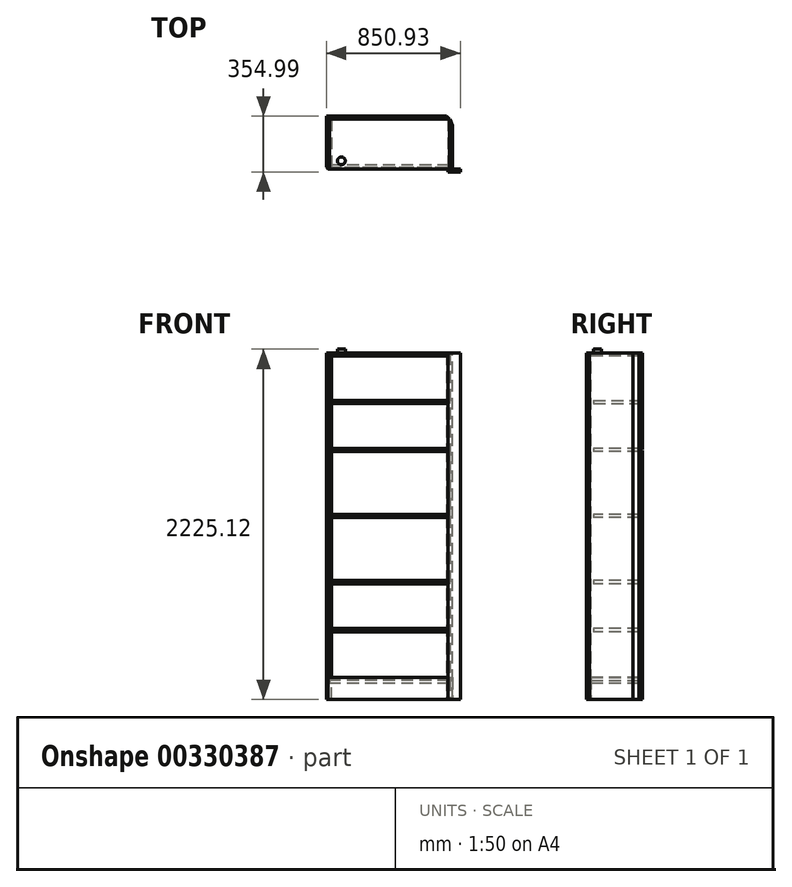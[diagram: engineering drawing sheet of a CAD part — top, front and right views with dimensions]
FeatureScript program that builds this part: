
annotation { "Feature Type Name" : "Feature", "Feature Type Description" : "" }
export const myFeature = defineFeature(function(context is Context, id is Id, definition is map)
    precondition{}
    {
        {
            var Q0;
            Q0=qCreatedBy(makeId("Right.planeOp"),FACE);
            var sketch = newSketch(context, id + "F0", { "sketchPlane" : qUnion([Q0])});
            skLineSegment(sketch, "E0.bottom", {"start": v(175, -1100) * mm, "end": v(-175, -1100) * mm});
            skLineSegment(sketch, "E0.top", {"start": v(175, 1100) * mm, "end": v(-175, 1100) * mm});
            skLineSegment(sketch, "E0.left", {"start": v(175, -1100) * mm, "end": v(175, 1100) * mm});
            skLineSegment(sketch, "E0.right", {"start": v(-175, -1100) * mm, "end": v(-175, 1100) * mm});
            skPoint(sketch, "E0.middle", {"position": v(0, 0) * mm});
            skSolve(sketch);
        }
        {
            var Q0;
            Q0=makeQuery(id+"F0.imprint","IMPRINT",FACE,{"disambiguationData":[TD([[makeQuery(id+"F0.imprint","IMPRINT",EDGE,{"derivedFrom":sQuery(id+"F0.wireOp",EDGE,"E0.bottom")}),-1.0]])]});
            extrude(context, id + "F1", {"entities" : qUnion([Q0]), "endBound" : BoundingType.SYMMETRIC, "depth" : 30 * mm});
        }
        {
            var Q0;
            Q0=makeQuery(id+"F1.opExtrude","SWEPT_BODY",BODY,{"disambiguationData":[OSD([sQuery(id+"F0.wireOp",EDGE,"E0.bottom"),sQuery(id+"F0.wireOp",EDGE,"E0.top"),sQuery(id+"F0.wireOp",EDGE,"E0.left"),sQuery(id+"F0.wireOp",EDGE,"E0.right")])]});
            transform(context, id + "F2", {"entities" : qUnion([Q0]), "transformType" : TransformType.TRANSLATION_3D, "dx" : -740 * mm, "dy" : 0 * mm, "dz" : 0 * mm, "makeCopy" : true});
        }
        {
            var Q0;
            Q0=makeQuery(id+"F2.opPattern","COPY",BODY,{"derivedFrom":makeQuery(id+"F1.opExtrude","SWEPT_BODY",BODY,{"disambiguationData":[OSD([sQuery(id+"F0.wireOp",EDGE,"E0.bottom"),sQuery(id+"F0.wireOp",EDGE,"E0.top"),sQuery(id+"F0.wireOp",EDGE,"E0.left"),sQuery(id+"F0.wireOp",EDGE,"E0.right")])]}),"instanceName":"1"});
            transform(context, id + "F3", {"entities" : qUnion([Q0]), "transformType" : TransformType.TRANSLATION_3D, "dx" : -30 * mm, "dy" : 0 * mm, "dz" : 0 * mm, "makeCopy" : false});
        }
        {
            var Q0;
            Q0=makeQuery(id+"F1.opExtrude","SWEPT_BODY",BODY,{"disambiguationData":[OSD([sQuery(id+"F0.wireOp",EDGE,"E0.bottom"),sQuery(id+"F0.wireOp",EDGE,"E0.top"),sQuery(id+"F0.wireOp",EDGE,"E0.left"),sQuery(id+"F0.wireOp",EDGE,"E0.right")])]});
            var Q1;
            Q1=makeQuery(id+"F2.opPattern","COPY",BODY,{"derivedFrom":makeQuery(id+"F1.opExtrude","SWEPT_BODY",BODY,{"disambiguationData":[OSD([sQuery(id+"F0.wireOp",EDGE,"E0.bottom"),sQuery(id+"F0.wireOp",EDGE,"E0.top"),sQuery(id+"F0.wireOp",EDGE,"E0.left"),sQuery(id+"F0.wireOp",EDGE,"E0.right")])]}),"instanceName":"1"});
            transform(context, id + "F4", {"entities" : qUnion([Q0, Q1]), "transformType" : TransformType.TRANSLATION_3D, "dx" : 385 * mm, "dy" : 0 * mm, "dz" : 0 * mm, "makeCopy" : false});
        }
        {
            var Q0;
            Q0=qCreatedBy(makeId("Top.planeOp"),FACE);
            var sketch = newSketch(context, id + "F5", { "sketchPlane" : qUnion([Q0])});
            skLineSegment(sketch, "E1.bottom", {"start": v(380, -175) * mm, "end": v(-380, -175) * mm});
            skLineSegment(sketch, "E1.top", {"start": v(380, 175) * mm, "end": v(-380, 175) * mm});
            skLineSegment(sketch, "E1.left", {"start": v(380, -175) * mm, "end": v(380, 175) * mm});
            skLineSegment(sketch, "E1.right", {"start": v(-380, -175) * mm, "end": v(-380, 175) * mm});
            skPoint(sketch, "E1.middle", {"position": v(0, 0) * mm});
            skSolve(sketch);
        }
        {
            var Q0;
            Q0=makeQuery(id+"F5.imprint","IMPRINT",FACE,{"disambiguationData":[TD([[makeQuery(id+"F5.imprint","IMPRINT",EDGE,{"derivedFrom":sQuery(id+"F5.wireOp",EDGE,"E1.bottom")}),-1.0]])]});
            extrude(context, id + "F6", {"entities" : qUnion([Q0]), "depth" : 20 * mm});
        }
        {
            var Q0;
            Q0=qCreatedBy(makeId("Top.planeOp"),FACE);
            var sketch = newSketch(context, id + "F7", { "sketchPlane" : qUnion([Q0])});
            skLineSegment(sketch, "E2.bottom", {"start": v(380, -175) * mm, "end": v(-380, -175) * mm});
            skLineSegment(sketch, "E2.top", {"start": v(380, 175) * mm, "end": v(-380, 175) * mm});
            skLineSegment(sketch, "E2.left", {"start": v(380, -175) * mm, "end": v(380, 175) * mm});
            skLineSegment(sketch, "E2.right", {"start": v(-380, -175) * mm, "end": v(-380, 175) * mm});
            skPoint(sketch, "E2.middle", {"position": v(0, 0) * mm});
            skSolve(sketch);
        }
        {
            var Q0;
            Q0=makeQuery(id+"F7.imprint","IMPRINT",FACE,{"disambiguationData":[TD([[makeQuery(id+"F7.imprint","IMPRINT",EDGE,{"derivedFrom":sQuery(id+"F7.wireOp",EDGE,"E2.bottom")}),-1.0]])]});
            extrude(context, id + "F8", {"entities" : qUnion([Q0]), "depth" : 20 * mm});
        }
        {
            var Q0;
            Q0=makeQuery(id+"F8.opExtrude","SWEPT_BODY",BODY,{"disambiguationData":[OSD([sQuery(id+"F7.wireOp",EDGE,"E2.bottom"),sQuery(id+"F7.wireOp",EDGE,"E2.top"),sQuery(id+"F7.wireOp",EDGE,"E2.left"),sQuery(id+"F7.wireOp",EDGE,"E2.right")])]});
            transform(context, id + "F9", {"entities" : qUnion([Q0]), "transformType" : TransformType.TRANSLATION_3D, "dx" : 0 * mm, "dy" : 0 * mm, "dz" : -980 * mm, "makeCopy" : false});
        }
        {
            var Q0;
            Q0=makeQuery(id+"F8.opExtrude","SWEPT_BODY",BODY,{"disambiguationData":[OSD([sQuery(id+"F7.wireOp",EDGE,"E2.bottom"),sQuery(id+"F7.wireOp",EDGE,"E2.top"),sQuery(id+"F7.wireOp",EDGE,"E2.left"),sQuery(id+"F7.wireOp",EDGE,"E2.right")])]});
            transform(context, id + "F10", {"entities" : qUnion([Q0]), "transformType" : TransformType.TRANSLATION_3D, "dx" : 0 * mm, "dy" : 0 * mm, "dz" : 300 * mm, "makeCopy" : false});
        }
        {
            var Q0;
            Q0=makeQuery(id+"F8.opExtrude","SWEPT_BODY",BODY,{"disambiguationData":[OSD([sQuery(id+"F7.wireOp",EDGE,"E2.bottom"),sQuery(id+"F7.wireOp",EDGE,"E2.top"),sQuery(id+"F7.wireOp",EDGE,"E2.left"),sQuery(id+"F7.wireOp",EDGE,"E2.right")])]});
            transform(context, id + "F11", {"entities" : qUnion([Q0]), "transformType" : TransformType.TRANSLATION_3D, "dx" : 0 * mm, "dy" : 0 * mm, "dz" : 400 * mm, "makeCopy" : false});
        }
        {
            var Q0;
            Q0=makeQuery(id+"F8.opExtrude","SWEPT_BODY",BODY,{"disambiguationData":[OSD([sQuery(id+"F7.wireOp",EDGE,"E2.bottom"),sQuery(id+"F7.wireOp",EDGE,"E2.top"),sQuery(id+"F7.wireOp",EDGE,"E2.left"),sQuery(id+"F7.wireOp",EDGE,"E2.right")])]});
            transform(context, id + "F12", {"entities" : qUnion([Q0]), "transformType" : TransformType.TRANSLATION_3D, "dx" : 0 * mm, "dy" : 0 * mm, "dz" : 300 * mm, "makeCopy" : false});
        }
        {
            var Q0;
            Q0=makeQuery(id+"F8.opExtrude","SWEPT_BODY",BODY,{"disambiguationData":[OSD([sQuery(id+"F7.wireOp",EDGE,"E2.bottom"),sQuery(id+"F7.wireOp",EDGE,"E2.top"),sQuery(id+"F7.wireOp",EDGE,"E2.left"),sQuery(id+"F7.wireOp",EDGE,"E2.right")])]});
            transform(context, id + "F13", {"entities" : qUnion([Q0]), "transformType" : TransformType.TRANSLATION_3D, "dx" : 0 * mm, "dy" : 0 * mm, "dz" : 300 * mm, "makeCopy" : false});
        }
        {
            var Q0;
            Q0=makeQuery(id+"F8.opExtrude","SWEPT_BODY",BODY,{"disambiguationData":[OSD([sQuery(id+"F7.wireOp",EDGE,"E2.bottom"),sQuery(id+"F7.wireOp",EDGE,"E2.top"),sQuery(id+"F7.wireOp",EDGE,"E2.left"),sQuery(id+"F7.wireOp",EDGE,"E2.right")])]});
            transform(context, id + "F14", {"entities" : qUnion([Q0]), "transformType" : TransformType.TRANSLATION_3D, "dx" : 0 * mm, "dy" : 0 * mm, "dz" : 400 * mm, "makeCopy" : false});
        }
        {
            var Q0;
            Q0=makeQuery(id+"F8.opExtrude","SWEPT_BODY",BODY,{"disambiguationData":[OSD([sQuery(id+"F7.wireOp",EDGE,"E2.bottom"),sQuery(id+"F7.wireOp",EDGE,"E2.top"),sQuery(id+"F7.wireOp",EDGE,"E2.left"),sQuery(id+"F7.wireOp",EDGE,"E2.right")])]});
            transform(context, id + "F15", {"entities" : qUnion([Q0]), "transformType" : TransformType.TRANSLATION_3D, "dx" : 0 * mm, "dy" : 0 * mm, "dz" : 360 * mm, "makeCopy" : false});
        }
        {
            var Q0;
            Q0=makeQuery(id+"F8.opExtrude","SWEPT_BODY",BODY,{"disambiguationData":[OSD([sQuery(id+"F7.wireOp",EDGE,"E2.bottom"),sQuery(id+"F7.wireOp",EDGE,"E2.top"),sQuery(id+"F7.wireOp",EDGE,"E2.left"),sQuery(id+"F7.wireOp",EDGE,"E2.right")])]});
            transform(context, id + "F16", {"entities" : qUnion([Q0]), "transformType" : TransformType.TRANSLATION_3D, "dx" : 0 * mm, "dy" : 0 * mm, "dz" : -2060 * mm, "makeCopy" : true});
        }
        {
            var Q0;
            Q0=makeQuery(id+"F6.opExtrude","SWEPT_BODY",BODY,{"disambiguationData":[OSD([sQuery(id+"F5.wireOp",EDGE,"E1.bottom"),sQuery(id+"F5.wireOp",EDGE,"E1.top"),sQuery(id+"F5.wireOp",EDGE,"E1.left"),sQuery(id+"F5.wireOp",EDGE,"E1.right")])]});
            transform(context, id + "F17", {"entities" : qUnion([Q0]), "transformType" : TransformType.TRANSLATION_3D, "dx" : 0 * mm, "dy" : 25 * mm, "dz" : 779.46 * mm, "makeCopy" : false});
        }
        {
            var Q0;
            Q0=makeQuery(id+"F8.opExtrude","SWEPT_BODY",BODY,{"disambiguationData":[OSD([sQuery(id+"F7.wireOp",EDGE,"E2.bottom"),sQuery(id+"F7.wireOp",EDGE,"E2.top"),sQuery(id+"F7.wireOp",EDGE,"E2.left"),sQuery(id+"F7.wireOp",EDGE,"E2.right")])]});
            var Q1;
            Q1=makeQuery(id+"F1.opExtrude","SWEPT_BODY",BODY,{"disambiguationData":[OSD([sQuery(id+"F0.wireOp",EDGE,"E0.bottom"),sQuery(id+"F0.wireOp",EDGE,"E0.top"),sQuery(id+"F0.wireOp",EDGE,"E0.left"),sQuery(id+"F0.wireOp",EDGE,"E0.right")])]});
            var Q2;
            Q2=makeQuery(id+"F2.opPattern","COPY",BODY,{"derivedFrom":makeQuery(id+"F1.opExtrude","SWEPT_BODY",BODY,{"disambiguationData":[OSD([sQuery(id+"F0.wireOp",EDGE,"E0.bottom"),sQuery(id+"F0.wireOp",EDGE,"E0.top"),sQuery(id+"F0.wireOp",EDGE,"E0.left"),sQuery(id+"F0.wireOp",EDGE,"E0.right")])]}),"instanceName":"1"});
            booleanBodies(context, id + "F18", {"operationType" : BooleanOperationType.SUBTRACTION, "tools" : qUnion([Q0]), "targets" : qUnion([Q1, Q2]), "keepTools" : true});
        }
        {
            var Q0;
            Q0=makeQuery(id+"F16.opPattern","COPY",BODY,{"derivedFrom":makeQuery(id+"F8.opExtrude","SWEPT_BODY",BODY,{"disambiguationData":[OSD([sQuery(id+"F7.wireOp",EDGE,"E2.bottom"),sQuery(id+"F7.wireOp",EDGE,"E2.top"),sQuery(id+"F7.wireOp",EDGE,"E2.left"),sQuery(id+"F7.wireOp",EDGE,"E2.right")])]}),"instanceName":"1"});
            var Q1;
            Q1=makeQuery(id+"F1.opExtrude","SWEPT_BODY",BODY,{"disambiguationData":[OSD([sQuery(id+"F0.wireOp",EDGE,"E0.bottom"),sQuery(id+"F0.wireOp",EDGE,"E0.top"),sQuery(id+"F0.wireOp",EDGE,"E0.left"),sQuery(id+"F0.wireOp",EDGE,"E0.right")])]});
            var Q2;
            Q2=makeQuery(id+"F2.opPattern","COPY",BODY,{"derivedFrom":makeQuery(id+"F1.opExtrude","SWEPT_BODY",BODY,{"disambiguationData":[OSD([sQuery(id+"F0.wireOp",EDGE,"E0.bottom"),sQuery(id+"F0.wireOp",EDGE,"E0.top"),sQuery(id+"F0.wireOp",EDGE,"E0.left"),sQuery(id+"F0.wireOp",EDGE,"E0.right")])]}),"instanceName":"1"});
            booleanBodies(context, id + "F19", {"operationType" : BooleanOperationType.SUBTRACTION, "tools" : qUnion([Q0]), "targets" : qUnion([Q1, Q2]), "keepTools" : true});
        }
        {
            var Q0;
            Q0=makeQuery(id+"F6.opExtrude","SWEPT_BODY",BODY,{"disambiguationData":[OSD([sQuery(id+"F5.wireOp",EDGE,"E1.bottom"),sQuery(id+"F5.wireOp",EDGE,"E1.top"),sQuery(id+"F5.wireOp",EDGE,"E1.left"),sQuery(id+"F5.wireOp",EDGE,"E1.right")])]});
            var Q1;
            Q1=makeQuery(id+"F1.opExtrude","SWEPT_BODY",BODY,{"disambiguationData":[OSD([sQuery(id+"F0.wireOp",EDGE,"E0.bottom"),sQuery(id+"F0.wireOp",EDGE,"E0.top"),sQuery(id+"F0.wireOp",EDGE,"E0.left"),sQuery(id+"F0.wireOp",EDGE,"E0.right")])]});
            var Q2;
            Q2=makeQuery(id+"F2.opPattern","COPY",BODY,{"derivedFrom":makeQuery(id+"F1.opExtrude","SWEPT_BODY",BODY,{"disambiguationData":[OSD([sQuery(id+"F0.wireOp",EDGE,"E0.bottom"),sQuery(id+"F0.wireOp",EDGE,"E0.top"),sQuery(id+"F0.wireOp",EDGE,"E0.left"),sQuery(id+"F0.wireOp",EDGE,"E0.right")])]}),"instanceName":"1"});
            booleanBodies(context, id + "F20", {"operationType" : BooleanOperationType.SUBTRACTION, "tools" : qUnion([Q0]), "targets" : qUnion([Q1, Q2]), "keepTools" : true});
        }
        {
            var Q0;
            Q0=makeQuery(id+"F6.opExtrude","SWEPT_BODY",BODY,{"disambiguationData":[OSD([sQuery(id+"F5.wireOp",EDGE,"E1.bottom"),sQuery(id+"F5.wireOp",EDGE,"E1.top"),sQuery(id+"F5.wireOp",EDGE,"E1.left"),sQuery(id+"F5.wireOp",EDGE,"E1.right")])]});
            transform(context, id + "F21", {"entities" : qUnion([Q0]), "transformType" : TransformType.TRANSLATION_3D, "dx" : 0 * mm, "dy" : 0 * mm, "dz" : -305 * mm, "makeCopy" : true});
        }
        {
            var Q0;
            Q0=makeQuery(id+"F21.opPattern","COPY",BODY,{"derivedFrom":makeQuery(id+"F6.opExtrude","SWEPT_BODY",BODY,{"disambiguationData":[OSD([sQuery(id+"F5.wireOp",EDGE,"E1.bottom"),sQuery(id+"F5.wireOp",EDGE,"E1.top"),sQuery(id+"F5.wireOp",EDGE,"E1.left"),sQuery(id+"F5.wireOp",EDGE,"E1.right")])]}),"instanceName":"1"});
            var Q1;
            Q1=makeQuery(id+"F2.opPattern","COPY",BODY,{"derivedFrom":makeQuery(id+"F1.opExtrude","SWEPT_BODY",BODY,{"disambiguationData":[OSD([sQuery(id+"F0.wireOp",EDGE,"E0.bottom"),sQuery(id+"F0.wireOp",EDGE,"E0.top"),sQuery(id+"F0.wireOp",EDGE,"E0.left"),sQuery(id+"F0.wireOp",EDGE,"E0.right")])]}),"instanceName":"1"});
            var Q2;
            Q2=makeQuery(id+"F1.opExtrude","SWEPT_BODY",BODY,{"disambiguationData":[OSD([sQuery(id+"F0.wireOp",EDGE,"E0.bottom"),sQuery(id+"F0.wireOp",EDGE,"E0.top"),sQuery(id+"F0.wireOp",EDGE,"E0.left"),sQuery(id+"F0.wireOp",EDGE,"E0.right")])]});
            booleanBodies(context, id + "F22", {"operationType" : BooleanOperationType.SUBTRACTION, "tools" : qUnion([Q0]), "targets" : qUnion([Q1, Q2]), "keepTools" : true});
        }
        {
            var Q0;
            Q0=makeQuery(id+"F21.opPattern","COPY",BODY,{"derivedFrom":makeQuery(id+"F6.opExtrude","SWEPT_BODY",BODY,{"disambiguationData":[OSD([sQuery(id+"F5.wireOp",EDGE,"E1.bottom"),sQuery(id+"F5.wireOp",EDGE,"E1.top"),sQuery(id+"F5.wireOp",EDGE,"E1.left"),sQuery(id+"F5.wireOp",EDGE,"E1.right")])]}),"instanceName":"1"});
            transform(context, id + "F23", {"entities" : qUnion([Q0]), "transformType" : TransformType.TRANSLATION_3D, "dx" : 0 * mm, "dy" : 0 * mm, "dz" : -420 * mm, "makeCopy" : true});
        }
        {
            var Q0;
            Q0=makeQuery(id+"F23.opPattern","COPY",BODY,{"derivedFrom":makeQuery(id+"F21.opPattern","COPY",BODY,{"derivedFrom":makeQuery(id+"F6.opExtrude","SWEPT_BODY",BODY,{"disambiguationData":[OSD([sQuery(id+"F5.wireOp",EDGE,"E1.bottom"),sQuery(id+"F5.wireOp",EDGE,"E1.top"),sQuery(id+"F5.wireOp",EDGE,"E1.left"),sQuery(id+"F5.wireOp",EDGE,"E1.right")])]}),"instanceName":"1"}),"instanceName":"1"});
            var Q1;
            Q1=makeQuery(id+"F2.opPattern","COPY",BODY,{"derivedFrom":makeQuery(id+"F1.opExtrude","SWEPT_BODY",BODY,{"disambiguationData":[OSD([sQuery(id+"F0.wireOp",EDGE,"E0.bottom"),sQuery(id+"F0.wireOp",EDGE,"E0.top"),sQuery(id+"F0.wireOp",EDGE,"E0.left"),sQuery(id+"F0.wireOp",EDGE,"E0.right")])]}),"instanceName":"1"});
            var Q2;
            Q2=makeQuery(id+"F1.opExtrude","SWEPT_BODY",BODY,{"disambiguationData":[OSD([sQuery(id+"F0.wireOp",EDGE,"E0.bottom"),sQuery(id+"F0.wireOp",EDGE,"E0.top"),sQuery(id+"F0.wireOp",EDGE,"E0.left"),sQuery(id+"F0.wireOp",EDGE,"E0.right")])]});
            booleanBodies(context, id + "F24", {"operationType" : BooleanOperationType.SUBTRACTION, "tools" : qUnion([Q0]), "targets" : qUnion([Q1, Q2]), "keepTools" : true});
        }
        {
            var Q0;
            Q0=makeQuery(id+"F23.opPattern","COPY",BODY,{"derivedFrom":makeQuery(id+"F21.opPattern","COPY",BODY,{"derivedFrom":makeQuery(id+"F6.opExtrude","SWEPT_BODY",BODY,{"disambiguationData":[OSD([sQuery(id+"F5.wireOp",EDGE,"E1.bottom"),sQuery(id+"F5.wireOp",EDGE,"E1.top"),sQuery(id+"F5.wireOp",EDGE,"E1.left"),sQuery(id+"F5.wireOp",EDGE,"E1.right")])]}),"instanceName":"1"}),"instanceName":"1"});
            transform(context, id + "F25", {"entities" : qUnion([Q0]), "transformType" : TransformType.TRANSLATION_3D, "dx" : 0 * mm, "dy" : 0 * mm, "dz" : -420 * mm, "makeCopy" : true});
        }
        {
            var Q0;
            Q0=makeQuery(id+"F25.opPattern","COPY",BODY,{"derivedFrom":makeQuery(id+"F23.opPattern","COPY",BODY,{"derivedFrom":makeQuery(id+"F21.opPattern","COPY",BODY,{"derivedFrom":makeQuery(id+"F6.opExtrude","SWEPT_BODY",BODY,{"disambiguationData":[OSD([sQuery(id+"F5.wireOp",EDGE,"E1.bottom"),sQuery(id+"F5.wireOp",EDGE,"E1.top"),sQuery(id+"F5.wireOp",EDGE,"E1.left"),sQuery(id+"F5.wireOp",EDGE,"E1.right")])]}),"instanceName":"1"}),"instanceName":"1"}),"instanceName":"1"});
            var Q1;
            Q1=makeQuery(id+"F1.opExtrude","SWEPT_BODY",BODY,{"disambiguationData":[OSD([sQuery(id+"F0.wireOp",EDGE,"E0.bottom"),sQuery(id+"F0.wireOp",EDGE,"E0.top"),sQuery(id+"F0.wireOp",EDGE,"E0.left"),sQuery(id+"F0.wireOp",EDGE,"E0.right")])]});
            var Q2;
            Q2=makeQuery(id+"F2.opPattern","COPY",BODY,{"derivedFrom":makeQuery(id+"F1.opExtrude","SWEPT_BODY",BODY,{"disambiguationData":[OSD([sQuery(id+"F0.wireOp",EDGE,"E0.bottom"),sQuery(id+"F0.wireOp",EDGE,"E0.top"),sQuery(id+"F0.wireOp",EDGE,"E0.left"),sQuery(id+"F0.wireOp",EDGE,"E0.right")])]}),"instanceName":"1"});
            booleanBodies(context, id + "F26", {"operationType" : BooleanOperationType.SUBTRACTION, "tools" : qUnion([Q0]), "targets" : qUnion([Q1, Q2]), "keepTools" : true});
        }
        {
            var Q0;
            Q0=makeQuery(id+"F25.opPattern","COPY",BODY,{"derivedFrom":makeQuery(id+"F23.opPattern","COPY",BODY,{"derivedFrom":makeQuery(id+"F21.opPattern","COPY",BODY,{"derivedFrom":makeQuery(id+"F6.opExtrude","SWEPT_BODY",BODY,{"disambiguationData":[OSD([sQuery(id+"F5.wireOp",EDGE,"E1.bottom"),sQuery(id+"F5.wireOp",EDGE,"E1.top"),sQuery(id+"F5.wireOp",EDGE,"E1.left"),sQuery(id+"F5.wireOp",EDGE,"E1.right")])]}),"instanceName":"1"}),"instanceName":"1"}),"instanceName":"1"});
            transform(context, id + "F27", {"entities" : qUnion([Q0]), "transformType" : TransformType.TRANSLATION_3D, "dx" : 0 * mm, "dy" : 0 * mm, "dz" : -305 * mm, "makeCopy" : true});
        }
        {
            var Q0;
            Q0=makeQuery(id+"F27.opPattern","COPY",BODY,{"derivedFrom":makeQuery(id+"F25.opPattern","COPY",BODY,{"derivedFrom":makeQuery(id+"F23.opPattern","COPY",BODY,{"derivedFrom":makeQuery(id+"F21.opPattern","COPY",BODY,{"derivedFrom":makeQuery(id+"F6.opExtrude","SWEPT_BODY",BODY,{"disambiguationData":[OSD([sQuery(id+"F5.wireOp",EDGE,"E1.bottom"),sQuery(id+"F5.wireOp",EDGE,"E1.top"),sQuery(id+"F5.wireOp",EDGE,"E1.left"),sQuery(id+"F5.wireOp",EDGE,"E1.right")])]}),"instanceName":"1"}),"instanceName":"1"}),"instanceName":"1"}),"instanceName":"1"});
            var Q1;
            Q1=makeQuery(id+"F1.opExtrude","SWEPT_BODY",BODY,{"disambiguationData":[OSD([sQuery(id+"F0.wireOp",EDGE,"E0.bottom"),sQuery(id+"F0.wireOp",EDGE,"E0.top"),sQuery(id+"F0.wireOp",EDGE,"E0.left"),sQuery(id+"F0.wireOp",EDGE,"E0.right")])]});
            var Q2;
            Q2=makeQuery(id+"F2.opPattern","COPY",BODY,{"derivedFrom":makeQuery(id+"F1.opExtrude","SWEPT_BODY",BODY,{"disambiguationData":[OSD([sQuery(id+"F0.wireOp",EDGE,"E0.bottom"),sQuery(id+"F0.wireOp",EDGE,"E0.top"),sQuery(id+"F0.wireOp",EDGE,"E0.left"),sQuery(id+"F0.wireOp",EDGE,"E0.right")])]}),"instanceName":"1"});
            booleanBodies(context, id + "F28", {"operationType" : BooleanOperationType.SUBTRACTION, "tools" : qUnion([Q0]), "targets" : qUnion([Q1, Q2]), "keepTools" : true});
        }
        {
            var Q0;
            Q0=qCreatedBy(makeId("Top.planeOp"),FACE);
            var sketch = newSketch(context, id + "F29", { "sketchPlane" : qUnion([Q0])});
            skLineSegment(sketch, "E3.bottom", {"start": v(-400.35, -200.02) * mm, "end": v(399.65, -200.02) * mm});
            skLineSegment(sketch, "E3.top", {"start": v(-400.35, -210.02) * mm, "end": v(399.65, -210.02) * mm});
            skLineSegment(sketch, "E3.left", {"start": v(-400.35, -200.02) * mm, "end": v(-400.35, -210.02) * mm});
            skLineSegment(sketch, "E3.right", {"start": v(399.65, -200.02) * mm, "end": v(399.65, -210.02) * mm});
            skSolve(sketch);
        }
        {
            var Q0;
            Q0 = qSketchRegion(id + "F29", true);
            extrude(context, id + "F30", {"entities" : qUnion([Q0]), "depth" : 140 * mm});
        }
        {
            var Q0;
            Q0=makeQuery(id+"F30.opExtrude","SWEPT_BODY",BODY,{"disambiguationData":[OSD([sQuery(id+"F29.wireOp",EDGE,"E3.bottom"),sQuery(id+"F29.wireOp",EDGE,"E3.top"),sQuery(id+"F29.wireOp",EDGE,"E3.left"),sQuery(id+"F29.wireOp",EDGE,"E3.right")])]});
            transform(context, id + "F31", {"entities" : qUnion([Q0]), "transformType" : TransformType.TRANSLATION_3D, "dx" : 0 * mm, "dy" : 15.02 * mm, "dz" : -1100 * mm, "makeCopy" : false});
        }
        {
            var Q0;
            Q0=makeQuery(id+"F30.opExtrude","SWEPT_BODY",BODY,{"disambiguationData":[OSD([sQuery(id+"F29.wireOp",EDGE,"E3.bottom"),sQuery(id+"F29.wireOp",EDGE,"E3.top"),sQuery(id+"F29.wireOp",EDGE,"E3.left"),sQuery(id+"F29.wireOp",EDGE,"E3.right")])]});
            transform(context, id + "F32", {"entities" : qUnion([Q0]), "transformType" : TransformType.TRANSLATION_3D, "dx" : 0 * mm, "dy" : 20 * mm, "dz" : 0 * mm, "makeCopy" : false});
        }
        {
            var Q0;
            Q0=makeQuery(id+"F30.opExtrude","SWEPT_BODY",BODY,{"disambiguationData":[OSD([sQuery(id+"F29.wireOp",EDGE,"E3.bottom"),sQuery(id+"F29.wireOp",EDGE,"E3.top"),sQuery(id+"F29.wireOp",EDGE,"E3.left"),sQuery(id+"F29.wireOp",EDGE,"E3.right")])]});
            var Q1;
            Q1=makeQuery(id+"F1.opExtrude","SWEPT_BODY",BODY,{"disambiguationData":[OSD([sQuery(id+"F0.wireOp",EDGE,"E0.bottom"),sQuery(id+"F0.wireOp",EDGE,"E0.top"),sQuery(id+"F0.wireOp",EDGE,"E0.left"),sQuery(id+"F0.wireOp",EDGE,"E0.right")])]});
            var Q2;
            Q2=makeQuery(id+"F2.opPattern","COPY",BODY,{"derivedFrom":makeQuery(id+"F1.opExtrude","SWEPT_BODY",BODY,{"disambiguationData":[OSD([sQuery(id+"F0.wireOp",EDGE,"E0.bottom"),sQuery(id+"F0.wireOp",EDGE,"E0.top"),sQuery(id+"F0.wireOp",EDGE,"E0.left"),sQuery(id+"F0.wireOp",EDGE,"E0.right")])]}),"instanceName":"1"});
            var Q3;
            Q3=makeQuery(id+"F16.opPattern","COPY",BODY,{"derivedFrom":makeQuery(id+"F8.opExtrude","SWEPT_BODY",BODY,{"disambiguationData":[OSD([sQuery(id+"F7.wireOp",EDGE,"E2.bottom"),sQuery(id+"F7.wireOp",EDGE,"E2.top"),sQuery(id+"F7.wireOp",EDGE,"E2.left"),sQuery(id+"F7.wireOp",EDGE,"E2.right")])]}),"instanceName":"1"});
            booleanBodies(context, id + "F33", {"operationType" : BooleanOperationType.SUBTRACTION, "tools" : qUnion([Q0]), "targets" : qUnion([Q1, Q2, Q3]), "keepTools" : true});
        }
        {
            var Q0;
            Q0=qCreatedBy(makeId("Top.planeOp"),FACE);
            var sketch = newSketch(context, id + "F34", { "sketchPlane" : qUnion([Q0])});
            skLineSegment(sketch, "E4.bottom", {"start": v(410.05, -199.99) * mm, "end": v(330.05, -199.99) * mm});
            skLineSegment(sketch, "E4.top", {"start": v(410.05, -219.99) * mm, "end": v(330.05, -219.99) * mm});
            skLineSegment(sketch, "E4.left", {"start": v(410.05, -199.99) * mm, "end": v(410.05, -219.99) * mm});
            skLineSegment(sketch, "E4.right", {"start": v(330.05, -199.99) * mm, "end": v(330.05, -219.99) * mm});
            skSolve(sketch);
        }
        {
            var Q0;
            Q0 = qSketchRegion(id + "F34", true);
            var Q1;
            Q1=makeQuery(id+"F8.opExtrude","CAP_FACE",FACE,{"disambiguationData":[OSD([sQuery(id+"F7.wireOp",EDGE,"E2.bottom"),sQuery(id+"F7.wireOp",EDGE,"E2.top"),sQuery(id+"F7.wireOp",EDGE,"E2.left"),sQuery(id+"F7.wireOp",EDGE,"E2.right")])],"isStart":false});
            var Q2;
            Q2=makeQuery(id+"F30.opExtrude","CAP_FACE",FACE,{"disambiguationData":[OSD([sQuery(id+"F29.wireOp",EDGE,"E3.bottom"),sQuery(id+"F29.wireOp",EDGE,"E3.top"),sQuery(id+"F29.wireOp",EDGE,"E3.left"),sQuery(id+"F29.wireOp",EDGE,"E3.right")])],"isStart":true});
            extrude(context, id + "F35", {"entities" : qUnion([Q0]), "endBound" : BoundingType.UP_TO_SURFACE, "endBoundEntityFace" : qUnion([Q1]), "depth" : 25 * mm, "hasSecondDirection" : true, "secondDirectionBound" : SecondDirectionBoundingType.UP_TO_SURFACE, "secondDirectionOppositeDirection" : true, "secondDirectionBoundEntityFace" : qUnion([Q2]), "secondDirectionDepth" : 25 * mm});
        }
        {
            var Q0;
            Q0=qCreatedBy(makeId("Top.planeOp"),FACE);
            var sketch = newSketch(context, id + "F36", { "sketchPlane" : qUnion([Q0])});
            skCircle(sketch, "E5", {"center": v(-335.94, -154.33) * mm, "radius": 25 * mm});
            skSolve(sketch);
        }
        {
            var Q0;
            Q0 = qSketchRegion(id + "F36", true);
            extrude(context, id + "F37", {"entities" : qUnion([Q0]), "depth" : 25 * mm});
        }
        {
            var Q0;
            Q0=makeQuery(id+"F37.opExtrude","SWEPT_BODY",BODY,{"disambiguationData":[OSD([sQuery(id+"F36.wireOp",EDGE,"E5")])]});
            transform(context, id + "F38", {"entities" : qUnion([Q0]), "transformType" : TransformType.TRANSLATION_3D, "dx" : 30 * mm, "dy" : 30 * mm, "dz" : 1100 * mm, "makeCopy" : false});
        }
        {
            var Q0;
            Q0=makeQuery(id+"F35.opExtrude","SWEPT_BODY",BODY,{"disambiguationData":[OSD([sQuery(id+"F34.wireOp",EDGE,"E4.bottom"),sQuery(id+"F34.wireOp",EDGE,"E4.top"),sQuery(id+"F34.wireOp",EDGE,"E4.left"),sQuery(id+"F34.wireOp",EDGE,"E4.right")])]});
            transform(context, id + "F39", {"entities" : qUnion([Q0]), "transformType" : TransformType.TRANSLATION_3D, "dx" : 40 * mm, "dy" : 25 * mm, "dz" : 0 * mm, "makeCopy" : false});
        }
        {
            var Q0;
            Q0=qCreatedBy(makeId("Top.planeOp"),FACE);
            var sketch = newSketch(context, id + "F40", { "sketchPlane" : qUnion([Q0])});
            skLineSegment(sketch, "E6.bottom", {"start": v(-402.2, 122.06) * mm, "end": v(418.1, 122.06) * mm});
            skLineSegment(sketch, "E6.top", {"start": v(-402.2, 62.06) * mm, "end": v(418.1, 62.06) * mm});
            skLineSegment(sketch, "E6.left", {"start": v(-402.2, 122.06) * mm, "end": v(-402.2, 62.06) * mm});
            skLineSegment(sketch, "E6.right", {"start": v(418.1, 122.06) * mm, "end": v(418.1, 62.06) * mm});
            skSolve(sketch);
        }
        {
            var Q0;
            Q0 = qSketchRegion(id + "F40", true);
            var Q1;
            Q1=makeQuery(id+"F8.opExtrude","CAP_FACE",FACE,{"disambiguationData":[OSD([sQuery(id+"F7.wireOp",EDGE,"E2.bottom"),sQuery(id+"F7.wireOp",EDGE,"E2.top"),sQuery(id+"F7.wireOp",EDGE,"E2.left"),sQuery(id+"F7.wireOp",EDGE,"E2.right")])],"isStart":false});
            var Q2;
            Q2=makeQuery(id+"F1.opExtrude","SWEPT_FACE",FACE,{"disambiguationData":[OSD([sQuery(id+"F0.wireOp",EDGE,"E0.bottom")])]});
            extrude(context, id + "F41", {"entities" : qUnion([Q0]), "endBound" : BoundingType.UP_TO_SURFACE, "endBoundEntityFace" : qUnion([Q1]), "depth" : 25 * mm, "hasSecondDirection" : true, "secondDirectionBound" : SecondDirectionBoundingType.UP_TO_SURFACE, "secondDirectionOppositeDirection" : true, "secondDirectionBoundEntityFace" : qUnion([Q2]), "secondDirectionDepth" : 25 * mm});
        }
        {
            var Q0;
            Q0=makeQuery(id+"F41.opExtrude","SWEPT_BODY",BODY,{"disambiguationData":[OSD([sQuery(id+"F40.wireOp",EDGE,"E6.bottom"),sQuery(id+"F40.wireOp",EDGE,"E6.top"),sQuery(id+"F40.wireOp",EDGE,"E6.left"),sQuery(id+"F40.wireOp",EDGE,"E6.right")])]});
            transform(context, id + "F42", {"entities" : qUnion([Q0]), "transformType" : TransformType.TRANSLATION_3D, "dx" : -8 * mm, "dy" : 78 * mm, "dz" : 0 * mm, "makeCopy" : false});
        }
        {
            var Q0;
            Q0=makeQuery(id+"F41.opExtrude","SWEPT_BODY",BODY,{"disambiguationData":[OSD([sQuery(id+"F40.wireOp",EDGE,"E6.bottom"),sQuery(id+"F40.wireOp",EDGE,"E6.top"),sQuery(id+"F40.wireOp",EDGE,"E6.left"),sQuery(id+"F40.wireOp",EDGE,"E6.right")])]});
            var Q1;
            Q1=makeQuery(id+"F1.opExtrude","SWEPT_BODY",BODY,{"disambiguationData":[OSD([sQuery(id+"F0.wireOp",EDGE,"E0.bottom"),sQuery(id+"F0.wireOp",EDGE,"E0.top"),sQuery(id+"F0.wireOp",EDGE,"E0.left"),sQuery(id+"F0.wireOp",EDGE,"E0.right")])]});
            var Q2;
            Q2=makeQuery(id+"F2.opPattern","COPY",BODY,{"derivedFrom":makeQuery(id+"F1.opExtrude","SWEPT_BODY",BODY,{"disambiguationData":[OSD([sQuery(id+"F0.wireOp",EDGE,"E0.bottom"),sQuery(id+"F0.wireOp",EDGE,"E0.top"),sQuery(id+"F0.wireOp",EDGE,"E0.left"),sQuery(id+"F0.wireOp",EDGE,"E0.right")])]}),"instanceName":"1"});
            var Q3;
            Q3=makeQuery(id+"F6.opExtrude","SWEPT_BODY",BODY,{"disambiguationData":[OSD([sQuery(id+"F5.wireOp",EDGE,"E1.bottom"),sQuery(id+"F5.wireOp",EDGE,"E1.top"),sQuery(id+"F5.wireOp",EDGE,"E1.left"),sQuery(id+"F5.wireOp",EDGE,"E1.right")])]});
            var Q4;
            Q4=makeQuery(id+"F8.opExtrude","SWEPT_BODY",BODY,{"disambiguationData":[OSD([sQuery(id+"F7.wireOp",EDGE,"E2.bottom"),sQuery(id+"F7.wireOp",EDGE,"E2.top"),sQuery(id+"F7.wireOp",EDGE,"E2.left"),sQuery(id+"F7.wireOp",EDGE,"E2.right")])]});
            var Q5;
            Q5=makeQuery(id+"F16.opPattern","COPY",BODY,{"derivedFrom":makeQuery(id+"F8.opExtrude","SWEPT_BODY",BODY,{"disambiguationData":[OSD([sQuery(id+"F7.wireOp",EDGE,"E2.bottom"),sQuery(id+"F7.wireOp",EDGE,"E2.top"),sQuery(id+"F7.wireOp",EDGE,"E2.left"),sQuery(id+"F7.wireOp",EDGE,"E2.right")])]}),"instanceName":"1"});
            var Q6;
            Q6=makeQuery(id+"F21.opPattern","COPY",BODY,{"derivedFrom":makeQuery(id+"F6.opExtrude","SWEPT_BODY",BODY,{"disambiguationData":[OSD([sQuery(id+"F5.wireOp",EDGE,"E1.bottom"),sQuery(id+"F5.wireOp",EDGE,"E1.top"),sQuery(id+"F5.wireOp",EDGE,"E1.left"),sQuery(id+"F5.wireOp",EDGE,"E1.right")])]}),"instanceName":"1"});
            var Q7;
            Q7=makeQuery(id+"F23.opPattern","COPY",BODY,{"derivedFrom":makeQuery(id+"F21.opPattern","COPY",BODY,{"derivedFrom":makeQuery(id+"F6.opExtrude","SWEPT_BODY",BODY,{"disambiguationData":[OSD([sQuery(id+"F5.wireOp",EDGE,"E1.bottom"),sQuery(id+"F5.wireOp",EDGE,"E1.top"),sQuery(id+"F5.wireOp",EDGE,"E1.left"),sQuery(id+"F5.wireOp",EDGE,"E1.right")])]}),"instanceName":"1"}),"instanceName":"1"});
            var Q8;
            Q8=makeQuery(id+"F25.opPattern","COPY",BODY,{"derivedFrom":makeQuery(id+"F23.opPattern","COPY",BODY,{"derivedFrom":makeQuery(id+"F21.opPattern","COPY",BODY,{"derivedFrom":makeQuery(id+"F6.opExtrude","SWEPT_BODY",BODY,{"disambiguationData":[OSD([sQuery(id+"F5.wireOp",EDGE,"E1.bottom"),sQuery(id+"F5.wireOp",EDGE,"E1.top"),sQuery(id+"F5.wireOp",EDGE,"E1.left"),sQuery(id+"F5.wireOp",EDGE,"E1.right")])]}),"instanceName":"1"}),"instanceName":"1"}),"instanceName":"1"});
            var Q9;
            Q9=makeQuery(id+"F27.opPattern","COPY",BODY,{"derivedFrom":makeQuery(id+"F25.opPattern","COPY",BODY,{"derivedFrom":makeQuery(id+"F23.opPattern","COPY",BODY,{"derivedFrom":makeQuery(id+"F21.opPattern","COPY",BODY,{"derivedFrom":makeQuery(id+"F6.opExtrude","SWEPT_BODY",BODY,{"disambiguationData":[OSD([sQuery(id+"F5.wireOp",EDGE,"E1.bottom"),sQuery(id+"F5.wireOp",EDGE,"E1.top"),sQuery(id+"F5.wireOp",EDGE,"E1.left"),sQuery(id+"F5.wireOp",EDGE,"E1.right")])]}),"instanceName":"1"}),"instanceName":"1"}),"instanceName":"1"}),"instanceName":"1"});
            booleanBodies(context, id + "F43", {"operationType" : BooleanOperationType.SUBTRACTION, "tools" : qUnion([Q0]), "targets" : qUnion([Q1, Q2, Q3, Q4, Q5, Q6, Q7, Q8, Q9])});
        }
        {
            var Q0;
            Q0=qCreatedBy(makeId("Front.planeOp"),FACE);
            var sketch = newSketch(context, id + "F44", { "sketchPlane" : qUnion([Q0])});
            skLineSegment(sketch, "E7.bottom", {"start": v(-400.13, 1099.06) * mm, "end": v(381.1, 1099.06) * mm});
            skLineSegment(sketch, "E7.top", {"start": v(-400.13, 486.73) * mm, "end": v(381.1, 486.73) * mm});
            skLineSegment(sketch, "E7.left", {"start": v(-400.13, 1099.06) * mm, "end": v(-400.13, 486.73) * mm});
            skLineSegment(sketch, "E7.right", {"start": v(381.1, 1099.06) * mm, "end": v(381.1, 486.73) * mm});
            skLineSegment(sketch, "E8.bottom", {"start": v(-400.88, 64.47) * mm, "end": v(381.4, 64.47) * mm});
            skLineSegment(sketch, "E8.top", {"start": v(-400.88, -1100.12) * mm, "end": v(381.4, -1100.12) * mm});
            skLineSegment(sketch, "E8.left", {"start": v(-400.88, 64.47) * mm, "end": v(-400.88, -1100.12) * mm});
            skLineSegment(sketch, "E8.right", {"start": v(381.4, 64.47) * mm, "end": v(381.4, -1100.12) * mm});
            skSolve(sketch);
        }
        {
            var Q0;
            Q0 = qSketchRegion(id + "F44", true);
            extrude(context, id + "F45", {"entities" : qUnion([Q0]), "depth" : 20 * mm});
        }
        {
            var Q0;
            Q0=makeQuery(id+"F45.opExtrude","SWEPT_BODY",BODY,{"disambiguationData":[OSD([sQuery(id+"F44.wireOp",EDGE,"E7.bottom"),sQuery(id+"F44.wireOp",EDGE,"E7.top"),sQuery(id+"F44.wireOp",EDGE,"E7.left"),sQuery(id+"F44.wireOp",EDGE,"E7.right")])]});
            var Q1;
            Q1=makeQuery(id+"F45.opExtrude","SWEPT_BODY",BODY,{"disambiguationData":[OSD([sQuery(id+"F44.wireOp",EDGE,"E8.bottom"),sQuery(id+"F44.wireOp",EDGE,"E8.top"),sQuery(id+"F44.wireOp",EDGE,"E8.left"),sQuery(id+"F44.wireOp",EDGE,"E8.right")])]});
            transform(context, id + "F46", {"entities" : qUnion([Q0, Q1]), "transformType" : TransformType.TRANSLATION_3D, "dx" : 0 * mm, "dy" : 160 * mm, "dz" : 0 * mm, "makeCopy" : false});
        }
        {
            var Q0;
            Q0=qCreatedBy(makeId("Front.planeOp"),FACE);
            var sketch = newSketch(context, id + "F47", { "sketchPlane" : qUnion([Q0])});
            skLineSegment(sketch, "E9.bottom", {"start": v(-400.57, 482.13) * mm, "end": v(380.97, 482.13) * mm});
            skLineSegment(sketch, "E9.top", {"start": v(-400.57, 66.6) * mm, "end": v(380.97, 66.6) * mm});
            skLineSegment(sketch, "E9.left", {"start": v(-400.57, 482.13) * mm, "end": v(-400.57, 66.6) * mm});
            skLineSegment(sketch, "E9.right", {"start": v(380.97, 482.13) * mm, "end": v(380.97, 66.6) * mm});
            skSolve(sketch);
        }
        {
            var Q0;
            Q0 = qSketchRegion(id + "F47", true);
            extrude(context, id + "F48", {"entities" : qUnion([Q0]), "depth" : 20 * mm});
        }
        {
            var Q0;
            Q0=makeQuery(id+"F48.opExtrude","SWEPT_BODY",BODY,{"disambiguationData":[OSD([sQuery(id+"F47.wireOp",EDGE,"E9.bottom"),sQuery(id+"F47.wireOp",EDGE,"E9.top"),sQuery(id+"F47.wireOp",EDGE,"E9.left"),sQuery(id+"F47.wireOp",EDGE,"E9.right")])]});
            transform(context, id + "F49", {"entities" : qUnion([Q0]), "transformType" : TransformType.TRANSLATION_3D, "dx" : 0 * mm, "dy" : 160 * mm, "dz" : 0 * mm, "makeCopy" : false});
        }
        {
            var Q0;
            Q0=makeQuery(id+"F45.opExtrude","CAP_EDGE",EDGE,{"disambiguationData":[OSD([sQuery(id+"F44.wireOp",EDGE,"E7.right")])],"isStart":true});
            var Q1;
            Q1=makeQuery(id+"F48.opExtrude","CAP_EDGE",EDGE,{"disambiguationData":[OSD([sQuery(id+"F47.wireOp",EDGE,"E9.right")])],"isStart":true});
            var Q2;
            Q2=makeQuery(id+"F45.opExtrude","CAP_EDGE",EDGE,{"disambiguationData":[OSD([sQuery(id+"F44.wireOp",EDGE,"E8.right")])],"isStart":true});
            chamfer(context, id + "F50", {"entities" : qUnion([Q0, Q1, Q2]), "chamferType" : ChamferType.OFFSET_ANGLE, "width" : 20 * mm, "oppositeDirection" : false, "angle" : 45 * degree, "tangentPropagation" : true});
        }
        {
            var Q0;
            Q0=makeQuery(id+"F30.opExtrude","SWEPT_BODY",BODY,{"disambiguationData":[OSD([sQuery(id+"F29.wireOp",EDGE,"E3.bottom"),sQuery(id+"F29.wireOp",EDGE,"E3.top"),sQuery(id+"F29.wireOp",EDGE,"E3.left"),sQuery(id+"F29.wireOp",EDGE,"E3.right")])]});
            var Q1;
            Q1=makeQuery(id+"F1.opExtrude","SWEPT_BODY",BODY,{"disambiguationData":[OSD([sQuery(id+"F0.wireOp",EDGE,"E0.bottom"),sQuery(id+"F0.wireOp",EDGE,"E0.top"),sQuery(id+"F0.wireOp",EDGE,"E0.left"),sQuery(id+"F0.wireOp",EDGE,"E0.right")])]});
            var Q2;
            Q2=makeQuery(id+"F2.opPattern","COPY",BODY,{"derivedFrom":makeQuery(id+"F1.opExtrude","SWEPT_BODY",BODY,{"disambiguationData":[OSD([sQuery(id+"F0.wireOp",EDGE,"E0.bottom"),sQuery(id+"F0.wireOp",EDGE,"E0.top"),sQuery(id+"F0.wireOp",EDGE,"E0.left"),sQuery(id+"F0.wireOp",EDGE,"E0.right")])]}),"instanceName":"1"});
            var Q3;
            Q3=makeQuery(id+"F16.opPattern","COPY",BODY,{"derivedFrom":makeQuery(id+"F8.opExtrude","SWEPT_BODY",BODY,{"disambiguationData":[OSD([sQuery(id+"F7.wireOp",EDGE,"E2.bottom"),sQuery(id+"F7.wireOp",EDGE,"E2.top"),sQuery(id+"F7.wireOp",EDGE,"E2.left"),sQuery(id+"F7.wireOp",EDGE,"E2.right")])]}),"instanceName":"1"});
            booleanBodies(context, id + "F51", {"operationType" : BooleanOperationType.SUBTRACTION, "tools" : qUnion([Q0]), "targets" : qUnion([Q1, Q2, Q3]), "keepTools" : true});
        }
        {
            var Q0;
            Q0=makeQuery(id+"F43.opBoolean","INTERSECT",EDGE,{"derivedFrom":[makeQuery(id+"F1.opExtrude","CAP_FACE",FACE,{"disambiguationData":[OSD([sQuery(id+"F0.wireOp",EDGE,"E0.bottom"),sQuery(id+"F0.wireOp",EDGE,"E0.top"),sQuery(id+"F0.wireOp",EDGE,"E0.left"),sQuery(id+"F0.wireOp",EDGE,"E0.right")])],"isStart":false}),makeQuery(id+"F41.opExtrude","SWEPT_FACE",FACE,{"disambiguationData":[OSD([sQuery(id+"F40.wireOp",EDGE,"E6.top")])]})]});
            chamfer(context, id + "F52", {"entities" : qUnion([Q0]), "chamferType" : ChamferType.OFFSET_ANGLE, "width" : 40 * mm, "oppositeDirection" : false, "angle" : 20 * degree, "tangentPropagation" : true});
        }
        {
            var Q0;
            Q0=makeQuery(id+"F2.opPattern","COPY",EDGE,{"derivedFrom":makeQuery(id+"F1.opExtrude","CAP_EDGE",EDGE,{"disambiguationData":[OSD([sQuery(id+"F0.wireOp",EDGE,"E0.right")])],"isStart":true}),"instanceName":"1"});
            var Q1;
            Q1=makeQuery(id+"F30.opExtrude","SWEPT_EDGE",EDGE,{"disambiguationData":[OSD([sQuery(id+"F29.wireOp",EDGE,"E3.top"),sQuery(id+"F29.wireOp",EDGE,"E3.left")])]});
            chamfer(context, id + "F53", {"entities" : qUnion([Q0, Q1]), "chamferType" : ChamferType.OFFSET_ANGLE, "width" : 10 * mm, "oppositeDirection" : false, "angle" : 45 * degree, "tangentPropagation" : true});
        }
        {
            var Q0;
            Q0=makeQuery(id+"F16.opPattern","COPY",BODY,{"derivedFrom":makeQuery(id+"F8.opExtrude","SWEPT_BODY",BODY,{"disambiguationData":[OSD([sQuery(id+"F7.wireOp",EDGE,"E2.bottom"),sQuery(id+"F7.wireOp",EDGE,"E2.top"),sQuery(id+"F7.wireOp",EDGE,"E2.left"),sQuery(id+"F7.wireOp",EDGE,"E2.right")])]}),"instanceName":"1"});
            transform(context, id + "F54", {"entities" : qUnion([Q0]), "transformType" : TransformType.TRANSLATION_3D, "dx" : 0 * mm, "dy" : 0 * mm, "dz" : -20 * mm, "makeCopy" : true});
        }
        {
            var Q0;
            Q0=makeQuery(id+"F54.opPattern","COPY",BODY,{"derivedFrom":makeQuery(id+"F16.opPattern","COPY",BODY,{"derivedFrom":makeQuery(id+"F8.opExtrude","SWEPT_BODY",BODY,{"disambiguationData":[OSD([sQuery(id+"F7.wireOp",EDGE,"E2.bottom"),sQuery(id+"F7.wireOp",EDGE,"E2.top"),sQuery(id+"F7.wireOp",EDGE,"E2.left"),sQuery(id+"F7.wireOp",EDGE,"E2.right")])]}),"instanceName":"1"}),"instanceName":"1"});
            var Q1;
            Q1=makeQuery(id+"F2.opPattern","COPY",BODY,{"derivedFrom":makeQuery(id+"F1.opExtrude","SWEPT_BODY",BODY,{"disambiguationData":[OSD([sQuery(id+"F0.wireOp",EDGE,"E0.bottom"),sQuery(id+"F0.wireOp",EDGE,"E0.top"),sQuery(id+"F0.wireOp",EDGE,"E0.left"),sQuery(id+"F0.wireOp",EDGE,"E0.right")])]}),"instanceName":"1"});
            var Q2;
            Q2=makeQuery(id+"F1.opExtrude","SWEPT_BODY",BODY,{"disambiguationData":[OSD([sQuery(id+"F0.wireOp",EDGE,"E0.bottom"),sQuery(id+"F0.wireOp",EDGE,"E0.top"),sQuery(id+"F0.wireOp",EDGE,"E0.left"),sQuery(id+"F0.wireOp",EDGE,"E0.right")])]});
            booleanBodies(context, id + "F55", {"operationType" : BooleanOperationType.SUBTRACTION, "tools" : qUnion([Q0]), "targets" : qUnion([Q1, Q2]), "keepTools" : true});
        }
    });
